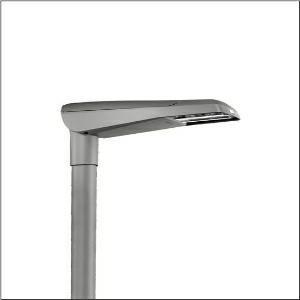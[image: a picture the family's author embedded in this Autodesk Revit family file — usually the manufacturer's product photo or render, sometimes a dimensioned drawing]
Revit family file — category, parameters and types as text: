
# Revit family: streetlight_sl_11_iq_micro___st0_5a_5xc1bc1f08ce_e478
name_source: partatom
category: Lighting Fixtures
units: mm (PartAtom-declared; Revit-internal decimal feet)

## family parameters
Cut with Voids When Loaded = No
Host = Face
Light Source = No
Part Type = Normal
Room Calculation Point = No
Round Connector Dimension = Use Diameter
Shared = No

## types (1)
- --- (1 x LED, 1580 lm, 14 W, 2200K)
    Apparent Load = 14 VA
    CIE Flux Codes = 42 72 97 100 100
    Color Rendering = 70
    Color Temperature = 2200K
    Default Elevation = 1800 mm
    Description = Streetlight SL 11 iQ micro, mast luminaire, primary light control with 3 zone facetted reflector, of plastic, silver coated, highly specular, primary optical cover: cover, of PMMA, transparent, light distribution: ST0.5a, light emission: direct distribution, primary light characteristic: asymmetric, installation type: post-top, side-entry, lamps: LED, High Power LED, rated values: 1.860lm | 13,8W | 134,8lm/W (begin service life); end service life: 1.860lm | 14W; at 50% lumin. flux: 930lm | 7,5W | 124lm/W, colour temperature: 2200/2700/3000/4000K, colour rendering: CRI > 70, light colour: 722/727/730/740, light setting 1 begin service life: 100% | 1.860lm | 13,8W | 134,8lm/W | 3.000K, light setting 1 end service life: 14W, further light settings possible, control: Street-Remote, Auto-Match, Temp-Guard, Lumen-Switch, Night-Set, Smart-Wire, Light-Fading, Desk-Remote (wireless, voltage-free reading and setting of iQ features in the workshop via application-optimized NFC function/RFID function), optimised constant luminous flux control (CLO 2.0), with cable H07RN-F 5x 1.5mm², mains connection: 220..240V, AC, 50/60Hz, connection cable pre-assembled, cable length: 5,5m, luminaire housing, of diecast aluminium, powder-coated, Siteco® metallic grey (DB 702S), please order mast flange separately, inclination adjustable without tools: 0°, 5°, 10°, 15° (post-top) | 0°, -5°, -10°, -15° (side-entry), sealing non-destructively replaceable, multi-level sealing system, length: 600mm, width: 174mm, height: 116mm, mast flange for spigot size: 42mm (side-entry): 5XC10008XM4, 60/48mm (side-entry/post-top): 5XC10108XM2, 76/60mm (side-entry/post-top): 5XC10108XM1, equipment: standard, protection rating (complete): IP66, insulation class (complete): insulation class II (safety insulation), certification: CE, ENEC, ENEC+, VDE, impact resistance: IK10, permissible operating ambient temperature for outdoor applications: -25..+50°C, standard-compliant lighting for roads and squares, Environmental Product Declaration (EPD) tested and certified by an independent institute, packaging unit: 1 piece

Light Distribution: ST0.5a
    Height = 116 mm
    Lamp = 1 x LED
    Lamp Light Flux = 1580 lm
    Lamp Power = 14 W
    Lamp count = 1
    Length = 600 mm
    Luminous efficacy = 113 lm/W
    Manufacturer = Siteco
    ModVariant = No
    Model = 5XC1BC1F08CE
    Number of Poles = 1
    OnlyDefault = Yes
    Power Factor = 1
    Product Name = Streetlight SL 11 iQ micro | ST0.5a
    Product group = mast luminaire | pylon top
    ProductGroupID = 6100
    Protection Class = Protection class II
    Protection Degree = IP 66
    RLX_Detail_Level = 1
    RLX_Emergency_Light_Flux = 0 lm
    RLX_Emergency_Type = 0
    RLX_Emergency_Type_DB = No
    RlxData = <blob elided: 58549 chars, md5=80c76268>
    Socket = socket
    Standby Power = 0 W
    System Light Flux = 1580 lm
    System Power = 14 W
    Type Comments = individual setting: luminous flux: 100 % | dim-lin: 254 | 369 mA
    Type Image = l_1006566.jpg
    URL = http://relux.com
    VarID = @adj_035920
    Voltage = 0 V
    Weight = 0.00 kg
    Width = 174 mm

## geometry (parser evidence)
native form markers: Blend x4, Sweep x10
no freeform markers — native parametric forms only
